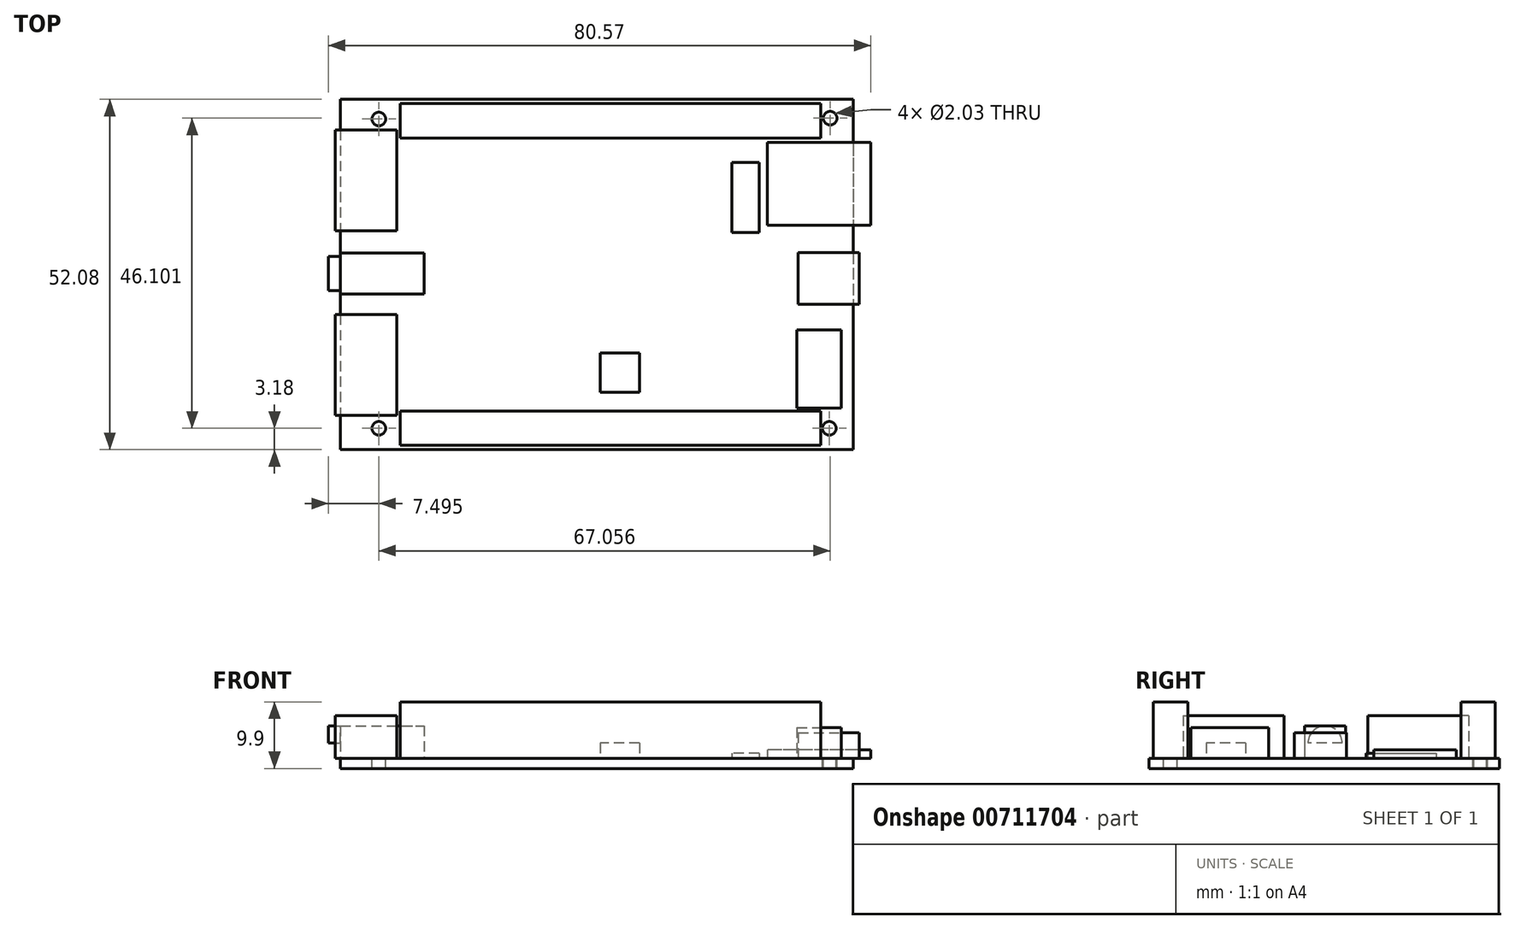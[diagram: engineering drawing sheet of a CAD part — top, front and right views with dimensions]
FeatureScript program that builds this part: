
annotation { "Feature Type Name" : "Feature", "Feature Type Description" : "" }
export const myFeature = defineFeature(function(context is Context, id is Id, definition is map)
    precondition{}
    {
        {
            var Q0;
            Q0=qCreatedBy(makeId("Top.planeOp"),FACE);
            var sketch = newSketch(context, id + "F0", { "sketchPlane" : qUnion([Q0])});
            skLineSegment(sketch, "E0.bottom", {"start": v(-38.1, 26.04) * mm, "end": v(38.1, 26.04) * mm});
            skLineSegment(sketch, "E0.top", {"start": v(-38.1, -26.04) * mm, "end": v(38.1, -26.04) * mm});
            skLineSegment(sketch, "E0.left", {"start": v(-38.1, 26.04) * mm, "end": v(-38.1, -26.04) * mm});
            skLineSegment(sketch, "E0.right", {"start": v(38.1, 26.04) * mm, "end": v(38.1, -26.04) * mm});
            skPoint(sketch, "E1", {"position": v(-32.39, 23.11) * mm});
            skPoint(sketch, "E2", {"position": v(34.67, 23.24) * mm});
            skPoint(sketch, "E3", {"position": v(-32.39, -22.86) * mm});
            skPoint(sketch, "E4", {"position": v(34.54, -22.86) * mm});
            skCircle(sketch, "E5", {"center": v(-32.39, 23.11) * mm, "radius": 1.02 * mm});
            skCircle(sketch, "E6", {"center": v(34.67, 23.24) * mm, "radius": 1.02 * mm});
            skCircle(sketch, "E7", {"center": v(34.54, -22.86) * mm, "radius": 1.02 * mm});
            skCircle(sketch, "E8", {"center": v(-32.39, -22.86) * mm, "radius": 1.02 * mm});
            skLineSegment(sketch, "E9.bottom", {"start": v(-29.21, 25.4) * mm, "end": v(33.27, 25.4) * mm});
            skLineSegment(sketch, "E9.top", {"start": v(-29.21, 20.27) * mm, "end": v(33.27, 20.27) * mm});
            skLineSegment(sketch, "E9.left", {"start": v(-29.21, 25.4) * mm, "end": v(-29.21, 20.27) * mm});
            skLineSegment(sketch, "E9.right", {"start": v(33.27, 25.4) * mm, "end": v(33.27, 20.27) * mm});
            skLineSegment(sketch, "E10.bottom", {"start": v(-29.21, -20.27) * mm, "end": v(33.27, -20.27) * mm});
            skLineSegment(sketch, "E10.top", {"start": v(-29.21, -25.4) * mm, "end": v(33.27, -25.4) * mm});
            skLineSegment(sketch, "E10.left", {"start": v(-29.21, -20.27) * mm, "end": v(-29.21, -25.4) * mm});
            skLineSegment(sketch, "E10.right", {"start": v(33.27, -20.27) * mm, "end": v(33.27, -25.4) * mm});
            skLineSegment(sketch, "E11.bottom", {"start": v(-38.86, -20.95) * mm, "end": v(-29.72, -20.95) * mm});
            skLineSegment(sketch, "E11.top", {"start": v(-38.86, -5.97) * mm, "end": v(-29.72, -5.97) * mm});
            skLineSegment(sketch, "E11.left", {"start": v(-38.86, -20.96) * mm, "end": v(-38.86, -5.97) * mm});
            skLineSegment(sketch, "E11.right", {"start": v(-29.72, -20.95) * mm, "end": v(-29.72, -5.97) * mm});
            skLineSegment(sketch, "E12.bottom", {"start": v(-29.72, 21.46) * mm, "end": v(-38.86, 21.46) * mm});
            skLineSegment(sketch, "E12.top", {"start": v(-29.72, 6.48) * mm, "end": v(-38.86, 6.48) * mm});
            skLineSegment(sketch, "E12.left", {"start": v(-29.72, 21.46) * mm, "end": v(-29.72, 6.48) * mm});
            skLineSegment(sketch, "E12.right", {"start": v(-38.86, 21.46) * mm, "end": v(-38.86, 6.48) * mm});
            skLineSegment(sketch, "E13.bottom", {"start": v(-39.88, 3.17) * mm, "end": v(-25.65, 3.17) * mm});
            skLineSegment(sketch, "E13.top", {"start": v(-39.88, -2.92) * mm, "end": v(-25.65, -2.92) * mm});
            skLineSegment(sketch, "E13.left", {"start": v(-39.88, 3.17) * mm, "end": v(-39.88, -2.92) * mm});
            skLineSegment(sketch, "E13.right", {"start": v(-25.65, 3.17) * mm, "end": v(-25.65, -2.92) * mm});
            skLineSegment(sketch, "E14.bottom", {"start": v(29.72, -8.25) * mm, "end": v(36.32, -8.25) * mm});
            skLineSegment(sketch, "E14.top", {"start": v(29.72, -19.86) * mm, "end": v(36.32, -19.86) * mm});
            skLineSegment(sketch, "E14.left", {"start": v(29.72, -8.25) * mm, "end": v(29.72, -19.86) * mm});
            skLineSegment(sketch, "E14.right", {"start": v(36.32, -8.25) * mm, "end": v(36.32, -19.86) * mm});
            skLineSegment(sketch, "E15.bottom", {"start": v(40.7, 19.63) * mm, "end": v(25.3, 19.63) * mm});
            skLineSegment(sketch, "E15.top", {"start": v(40.7, 7.32) * mm, "end": v(25.3, 7.32) * mm});
            skLineSegment(sketch, "E15.left", {"start": v(40.7, 19.63) * mm, "end": v(40.7, 7.32) * mm});
            skLineSegment(sketch, "E15.right", {"start": v(25.3, 19.63) * mm, "end": v(25.3, 7.32) * mm});
            skLineSegment(sketch, "E16.bottom", {"start": v(29.92, 3.25) * mm, "end": v(38.99, 3.25) * mm});
            skLineSegment(sketch, "E16.top", {"start": v(29.92, -4.44) * mm, "end": v(38.99, -4.44) * mm});
            skLineSegment(sketch, "E16.left", {"start": v(29.92, 3.25) * mm, "end": v(29.92, -4.44) * mm});
            skLineSegment(sketch, "E16.right", {"start": v(38.99, 3.25) * mm, "end": v(38.99, -4.44) * mm});
            skPoint(sketch, "E17", {"position": v(3.43, -14.6) * mm});
            skLineSegment(sketch, "E18.bottom", {"start": v(6.35, -11.68) * mm, "end": v(0.5, -11.68) * mm});
            skLineSegment(sketch, "E18.top", {"start": v(6.35, -17.53) * mm, "end": v(0.5, -17.53) * mm});
            skLineSegment(sketch, "E18.left", {"start": v(6.35, -11.68) * mm, "end": v(6.35, -17.53) * mm});
            skLineSegment(sketch, "E18.right", {"start": v(0.5, -11.68) * mm, "end": v(0.5, -17.53) * mm});
            skLineSegment(sketch, "E19.bottom", {"start": v(24.13, 6.22) * mm, "end": v(20.07, 6.22) * mm});
            skLineSegment(sketch, "E19.top", {"start": v(24.13, 16.64) * mm, "end": v(20.07, 16.64) * mm});
            skLineSegment(sketch, "E19.left", {"start": v(24.13, 6.22) * mm, "end": v(24.13, 16.64) * mm});
            skLineSegment(sketch, "E19.right", {"start": v(20.07, 6.22) * mm, "end": v(20.07, 16.64) * mm});
            skPoint(sketch, "E19.middle", {"position": v(22.1, 11.43) * mm});
            skPoint(sketch, "E20", {"position": v(-25.65, 0.13) * mm});
            skSolve(sketch);
        }
        {
            var Q0;
            {var subQ12=sQuery(id+"F0.wireOp",EDGE,"E0.bottom");Q0=makeQuery(id+"F0.imprint","IMPRINT",FACE,{"disambiguationData":[TD([[makeQuery(id+"F0.imprint","IMPRINT",EDGE,{"derivedFrom":subQ12}),-1.0]])]});}
            var Q1;
            Q1=makeQuery(id+"F0.imprint","IMPRINT",FACE,{"disambiguationData":[TD([[makeQuery(id+"F0.imprint","IMPRINT",EDGE,{"derivedFrom":sQuery(id+"F0.wireOp",EDGE,"E9.bottom")}),-1.0]])]});
            var Q2;
            {var subQ5=sQuery(id+"F0.wireOp",EDGE,"E15.right");Q2=makeQuery(id+"F0.imprint","IMPRINT",FACE,{"disambiguationData":[TD([[makeQuery(id+"F0.imprint","IMPRINT",EDGE,{"derivedFrom":subQ5}),1.0]])]});}
            var Q3;
            {var subQ5=sQuery(id+"F0.wireOp",EDGE,"E16.left");Q3=makeQuery(id+"F0.imprint","IMPRINT",FACE,{"disambiguationData":[TD([[makeQuery(id+"F0.imprint","IMPRINT",EDGE,{"derivedFrom":subQ5}),1.0]])]});}
            var Q4;
            Q4=makeQuery(id+"F0.imprint","IMPRINT",FACE,{"disambiguationData":[TD([[makeQuery(id+"F0.imprint","IMPRINT",EDGE,{"derivedFrom":sQuery(id+"F0.wireOp",EDGE,"E14.bottom")}),-1.0]])]});
            var Q5;
            Q5=makeQuery(id+"F0.imprint","IMPRINT",FACE,{"disambiguationData":[TD([[makeQuery(id+"F0.imprint","IMPRINT",EDGE,{"derivedFrom":sQuery(id+"F0.wireOp",EDGE,"E10.bottom")}),-1.0]])]});
            var Q6;
            Q6=makeQuery(id+"F0.imprint","IMPRINT",FACE,{"disambiguationData":[TD([[makeQuery(id+"F0.imprint","IMPRINT",EDGE,{"derivedFrom":sQuery(id+"F0.wireOp",EDGE,"E18.bottom")}),1.0]])]});
            var Q7;
            {var subQ5=sQuery(id+"F0.wireOp",EDGE,"E11.right");Q7=makeQuery(id+"F0.imprint","IMPRINT",FACE,{"disambiguationData":[TD([[makeQuery(id+"F0.imprint","IMPRINT",EDGE,{"derivedFrom":subQ5}),1.0]])]});}
            var Q8;
            {var subQ5=sQuery(id+"F0.wireOp",EDGE,"E13.right");Q8=makeQuery(id+"F0.imprint","IMPRINT",FACE,{"disambiguationData":[TD([[makeQuery(id+"F0.imprint","IMPRINT",EDGE,{"derivedFrom":subQ5}),-1.0]])]});}
            var Q9;
            {var subQ5=sQuery(id+"F0.wireOp",EDGE,"E12.left");Q9=makeQuery(id+"F0.imprint","IMPRINT",FACE,{"disambiguationData":[TD([[makeQuery(id+"F0.imprint","IMPRINT",EDGE,{"derivedFrom":subQ5}),-1.0]])]});}
            var Q10;
            Q10=makeQuery(id+"F0.imprint","IMPRINT",FACE,{"disambiguationData":[TD([[makeQuery(id+"F0.imprint","IMPRINT",EDGE,{"derivedFrom":sQuery(id+"F0.wireOp",EDGE,"E19.bottom")}),-1.0]])]});
            extrude(context, id + "F1", {"entities" : qUnion([Q0, Q1, Q2, Q3, Q4, Q5, Q6, Q7, Q8, Q9, Q10]), "oppositeDirection" : true, "depth" : 1.52 * mm, "offsetDistance" : 25.4 * mm});
        }
        {
            var Q0;
            Q0=makeQuery(id+"F0.imprint","IMPRINT",FACE,{"disambiguationData":[TD([[makeQuery(id+"F0.imprint","IMPRINT",EDGE,{"derivedFrom":sQuery(id+"F0.wireOp",EDGE,"E9.bottom")}),-1.0]])]});
            var Q1;
            Q1=makeQuery(id+"F0.imprint","IMPRINT",FACE,{"disambiguationData":[TD([[makeQuery(id+"F0.imprint","IMPRINT",EDGE,{"derivedFrom":sQuery(id+"F0.wireOp",EDGE,"E10.bottom")}),-1.0]])]});
            extrude(context, id + "F2", {"entities" : qUnion([Q0, Q1]), "operationType" : NewBodyOperationType.ADD, "depth" : 8.38 * mm, "offsetDistance" : 25.4 * mm});
        }
        {
            var Q0;
            {var subQ5=sQuery(id+"F0.wireOp",EDGE,"E12.left");Q0=makeQuery(id+"F0.imprint","IMPRINT",FACE,{"disambiguationData":[TD([[makeQuery(id+"F0.imprint","IMPRINT",EDGE,{"derivedFrom":subQ5}),-1.0]])]});}
            var Q1;
            {var subQ5=sQuery(id+"F0.wireOp",EDGE,"E12.right");Q1=makeQuery(id+"F0.imprint","IMPRINT",FACE,{"disambiguationData":[TD([[makeQuery(id+"F0.imprint","IMPRINT",EDGE,{"derivedFrom":subQ5}),1.0]])]});}
            var Q2;
            {var subQ5=sQuery(id+"F0.wireOp",EDGE,"E11.left");Q2=makeQuery(id+"F0.imprint","IMPRINT",FACE,{"disambiguationData":[TD([[makeQuery(id+"F0.imprint","IMPRINT",EDGE,{"derivedFrom":subQ5}),-1.0]])]});}
            var Q3;
            {var subQ5=sQuery(id+"F0.wireOp",EDGE,"E11.right");Q3=makeQuery(id+"F0.imprint","IMPRINT",FACE,{"disambiguationData":[TD([[makeQuery(id+"F0.imprint","IMPRINT",EDGE,{"derivedFrom":subQ5}),1.0]])]});}
            extrude(context, id + "F3", {"entities" : qUnion([Q0, Q1, Q2, Q3]), "operationType" : NewBodyOperationType.ADD, "depth" : 6.35 * mm, "offsetDistance" : 25.4 * mm});
        }
        {
            var Q0;
            {var subQ5=sQuery(id+"F0.wireOp",EDGE,"E13.right");Q0=makeQuery(id+"F0.imprint","IMPRINT",FACE,{"disambiguationData":[TD([[makeQuery(id+"F0.imprint","IMPRINT",EDGE,{"derivedFrom":subQ5}),-1.0]])]});}
            extrude(context, id + "F4", {"entities" : qUnion([Q0]), "operationType" : NewBodyOperationType.ADD, "depth" : 4.83 * mm, "offsetDistance" : 25.4 * mm});
        }
        {
            var Q0;
            Q0=makeQuery(id+"F0.imprint","IMPRINT",FACE,{"disambiguationData":[TD([[makeQuery(id+"F0.imprint","IMPRINT",EDGE,{"derivedFrom":sQuery(id+"F0.wireOp",EDGE,"E18.bottom")}),1.0]])]});
            extrude(context, id + "F5", {"entities" : qUnion([Q0]), "operationType" : NewBodyOperationType.ADD, "depth" : 2.3 * mm, "offsetDistance" : 25.4 * mm});
        }
        {
            var Q0;
            {var subQ5=sQuery(id+"F0.wireOp",EDGE,"E15.right");Q0=makeQuery(id+"F0.imprint","IMPRINT",FACE,{"disambiguationData":[TD([[makeQuery(id+"F0.imprint","IMPRINT",EDGE,{"derivedFrom":subQ5}),1.0]])]});}
            var Q1;
            {var subQ5=sQuery(id+"F0.wireOp",EDGE,"E15.left");Q1=makeQuery(id+"F0.imprint","IMPRINT",FACE,{"disambiguationData":[TD([[makeQuery(id+"F0.imprint","IMPRINT",EDGE,{"derivedFrom":subQ5}),-1.0]])]});}
            extrude(context, id + "F6", {"entities" : qUnion([Q0, Q1]), "operationType" : NewBodyOperationType.ADD, "depth" : 1.27 * mm, "offsetDistance" : 25.4 * mm});
        }
        {
            var Q0;
            {var subQ5=sQuery(id+"F0.wireOp",EDGE,"E16.left");Q0=makeQuery(id+"F0.imprint","IMPRINT",FACE,{"disambiguationData":[TD([[makeQuery(id+"F0.imprint","IMPRINT",EDGE,{"derivedFrom":subQ5}),1.0]])]});}
            var Q1;
            {var subQ5=sQuery(id+"F0.wireOp",EDGE,"E16.right");Q1=makeQuery(id+"F0.imprint","IMPRINT",FACE,{"disambiguationData":[TD([[makeQuery(id+"F0.imprint","IMPRINT",EDGE,{"derivedFrom":subQ5}),-1.0]])]});}
            extrude(context, id + "F7", {"entities" : qUnion([Q0, Q1]), "operationType" : NewBodyOperationType.ADD, "depth" : 3.8 * mm, "offsetDistance" : 25.4 * mm});
        }
        {
            var Q0;
            Q0=makeQuery(id+"F0.imprint","IMPRINT",FACE,{"disambiguationData":[TD([[makeQuery(id+"F0.imprint","IMPRINT",EDGE,{"derivedFrom":sQuery(id+"F0.wireOp",EDGE,"E14.bottom")}),-1.0]])]});
            extrude(context, id + "F8", {"entities" : qUnion([Q0]), "operationType" : NewBodyOperationType.ADD, "depth" : 4.57 * mm, "offsetDistance" : 25.4 * mm});
        }
        {
            var Q0;
            Q0=makeQuery(id+"F0.imprint","IMPRINT",FACE,{"disambiguationData":[TD([[makeQuery(id+"F0.imprint","IMPRINT",EDGE,{"derivedFrom":sQuery(id+"F0.wireOp",EDGE,"E19.bottom")}),-1.0]])]});
            extrude(context, id + "F9", {"entities" : qUnion([Q0]), "operationType" : NewBodyOperationType.ADD, "depth" : 0.76 * mm, "offsetDistance" : 25.4 * mm});
        }
        {
            var Q0;
            {var subQ0=sQuery(id+"F0.wireOp",EDGE,"E0.left");Q0=makeQuery(id+"F4.boolean.opBoolean","MERGE",FACE,{"derivedFrom":[makeQuery(id+"F1.opExtrude","SWEPT_FACE",FACE,{"disambiguationData":[OSD([subQ0])]}),makeQuery(id+"F4.opExtrude","SWEPT_FACE",FACE,{"disambiguationData":[OSD([subQ0])]})]});}
            var sketch = newSketch(context, id + "F10", { "sketchPlane" : qUnion([Q0])});
            skCircle(sketch, "E21", {"center": v(-0.13, 2.29) * mm, "radius": 2.54 * mm});
            skLineSegment(sketch, "E22", {"start": v(-3.17, 2.29) * mm, "end": v(2.92, 2.29) * mm});
            skLineSegment(sketch, "E23", {"start": v(-0.13, 2.29) * mm, "end": v(-0.13, 4.83) * mm});
            skSolve(sketch);
        }
        {
            var Q0;
            {var subQ0=sQuery(id+"F10.wireOp",EDGE,"E23");Q0=makeQuery(id+"F10.imprint","IMPRINT",FACE,{"disambiguationData":[TD([[makeQuery(id+"F10.imprint","IMPRINT",EDGE,{"derivedFrom":subQ0}),-1.0]])]});}
            var Q1;
            {var subQ0=sQuery(id+"F10.wireOp",EDGE,"E23");Q1=makeQuery(id+"F10.imprint","IMPRINT",FACE,{"disambiguationData":[TD([[makeQuery(id+"F10.imprint","IMPRINT",EDGE,{"derivedFrom":subQ0}),1.0]])]});}
            var Q2;
            {var subQ0=sQuery(id+"F10.wireOp",EDGE,"E22");var subQ1=sQuery(id+"F10.wireOp",EDGE,"E21");var subQ2=makeQuery(id+"F10.imprint","INTERSECT",VERTEX,{"disambiguationData":[OD(0.0)],"derivedFrom":[subQ1,subQ0]});Q2=makeQuery(id+"F10.imprint","IMPRINT",FACE,{"disambiguationData":[TD([[makeQuery(id+"F10.imprint","IMPRINT",EDGE,{"disambiguationData":[TD([[subQ2,1.0]])],"derivedFrom":subQ1}),1.0]])]});}
            extrude(context, id + "F11", {"entities" : qUnion([Q0, Q1, Q2]), "operationType" : NewBodyOperationType.ADD, "depth" : 1.78 * mm, "offsetDistance" : 25.4 * mm});
        }
    });
